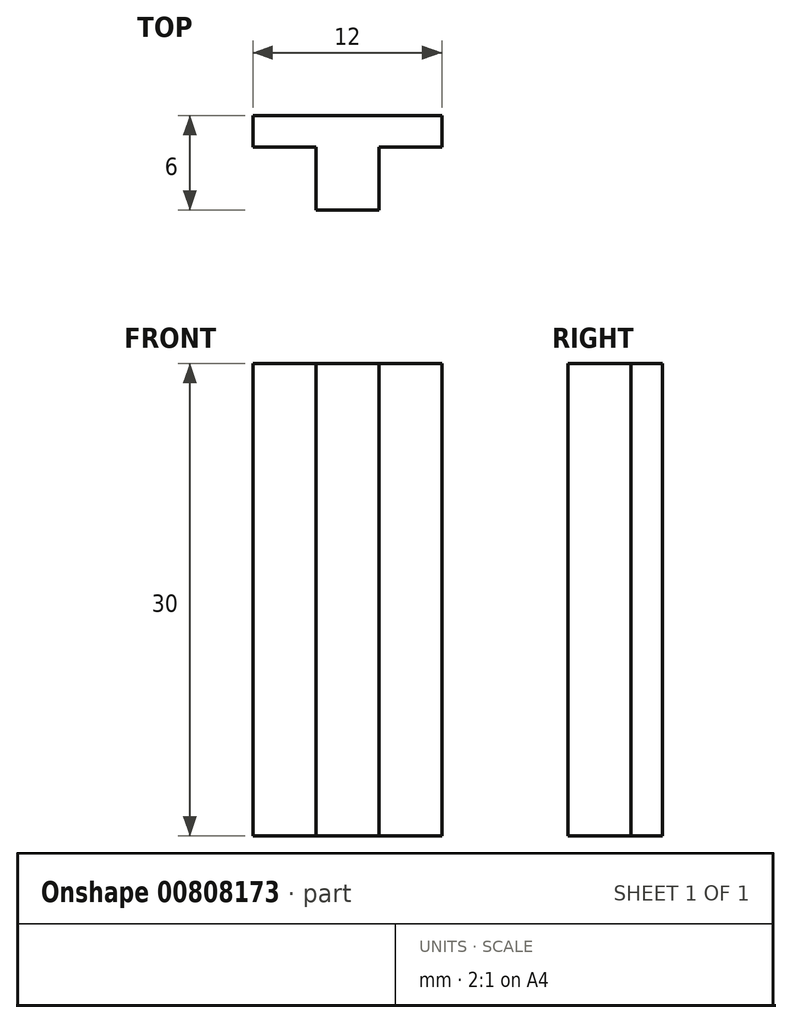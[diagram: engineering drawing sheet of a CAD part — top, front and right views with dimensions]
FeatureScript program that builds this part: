
annotation { "Feature Type Name" : "Feature", "Feature Type Description" : "" }
export const myFeature = defineFeature(function(context is Context, id is Id, definition is map)
    precondition{}
    {
        {
            var Q0;
            Q0=qCreatedBy(makeId("Top.planeOp"),FACE);
            var sketch = newSketch(context, id + "F0", { "sketchPlane" : qUnion([Q0])});
            skLineSegment(sketch, "E0.bottom", {"start": v(-2, 0) * mm, "end": v(2, 0) * mm});
            skLineSegment(sketch, "E0.top", {"start": v(-2, 6) * mm, "end": v(2, 6) * mm});
            skLineSegment(sketch, "E0.left", {"start": v(-2, 0) * mm, "end": v(-2, 6) * mm});
            skLineSegment(sketch, "E0.right", {"start": v(2, 0) * mm, "end": v(2, 6) * mm});
            skLineSegment(sketch, "E1.bottom", {"start": v(0, 6) * mm, "end": v(6, 6) * mm});
            skLineSegment(sketch, "E1.top", {"start": v(0, 4) * mm, "end": v(6, 4) * mm});
            skLineSegment(sketch, "E1.left", {"start": v(0, 6) * mm, "end": v(0, 4) * mm});
            skLineSegment(sketch, "E1.right", {"start": v(6, 6) * mm, "end": v(6, 4) * mm});
            skLineSegment(sketch, "E2.bottom", {"start": v(0, 6) * mm, "end": v(-6, 6) * mm});
            skLineSegment(sketch, "E2.top", {"start": v(0, 4) * mm, "end": v(-6, 4) * mm});
            skLineSegment(sketch, "E2.right", {"start": v(-6, 6) * mm, "end": v(-6, 4) * mm});
            skSolve(sketch);
        }
        {
            var Q0;
            {var subQ5=sQuery(id+"F0.wireOp",EDGE,"E1.left");Q0=makeQuery(id+"F0.imprint","IMPRINT",FACE,{"disambiguationData":[TD([[makeQuery(id+"F0.imprint","IMPRINT",EDGE,{"derivedFrom":subQ5}),-1.0]])]});}
            var Q1;
            {var subQ5=sQuery(id+"F0.wireOp",EDGE,"E1.left");Q1=makeQuery(id+"F0.imprint","IMPRINT",FACE,{"disambiguationData":[TD([[makeQuery(id+"F0.imprint","IMPRINT",EDGE,{"derivedFrom":subQ5}),1.0]])]});}
            var Q2;
            {var subQ5=sQuery(id+"F0.wireOp",EDGE,"E1.right");Q2=makeQuery(id+"F0.imprint","IMPRINT",FACE,{"disambiguationData":[TD([[makeQuery(id+"F0.imprint","IMPRINT",EDGE,{"derivedFrom":subQ5}),-1.0]])]});}
            var Q3;
            {var subQ5=sQuery(id+"F0.wireOp",EDGE,"E0.bottom");Q3=makeQuery(id+"F0.imprint","IMPRINT",FACE,{"disambiguationData":[TD([[makeQuery(id+"F0.imprint","IMPRINT",EDGE,{"derivedFrom":subQ5}),1.0]])]});}
            var Q4;
            {var subQ5=sQuery(id+"F0.wireOp",EDGE,"E2.right");Q4=makeQuery(id+"F0.imprint","IMPRINT",FACE,{"disambiguationData":[TD([[makeQuery(id+"F0.imprint","IMPRINT",EDGE,{"derivedFrom":subQ5}),1.0]])]});}
            extrude(context, id + "F1", {"entities" : qUnion([Q0, Q1, Q2, Q3, Q4]), "endBound" : BoundingType.SYMMETRIC, "depth" : 30 * mm, "offsetDistance" : 25 * mm});
        }
    });
